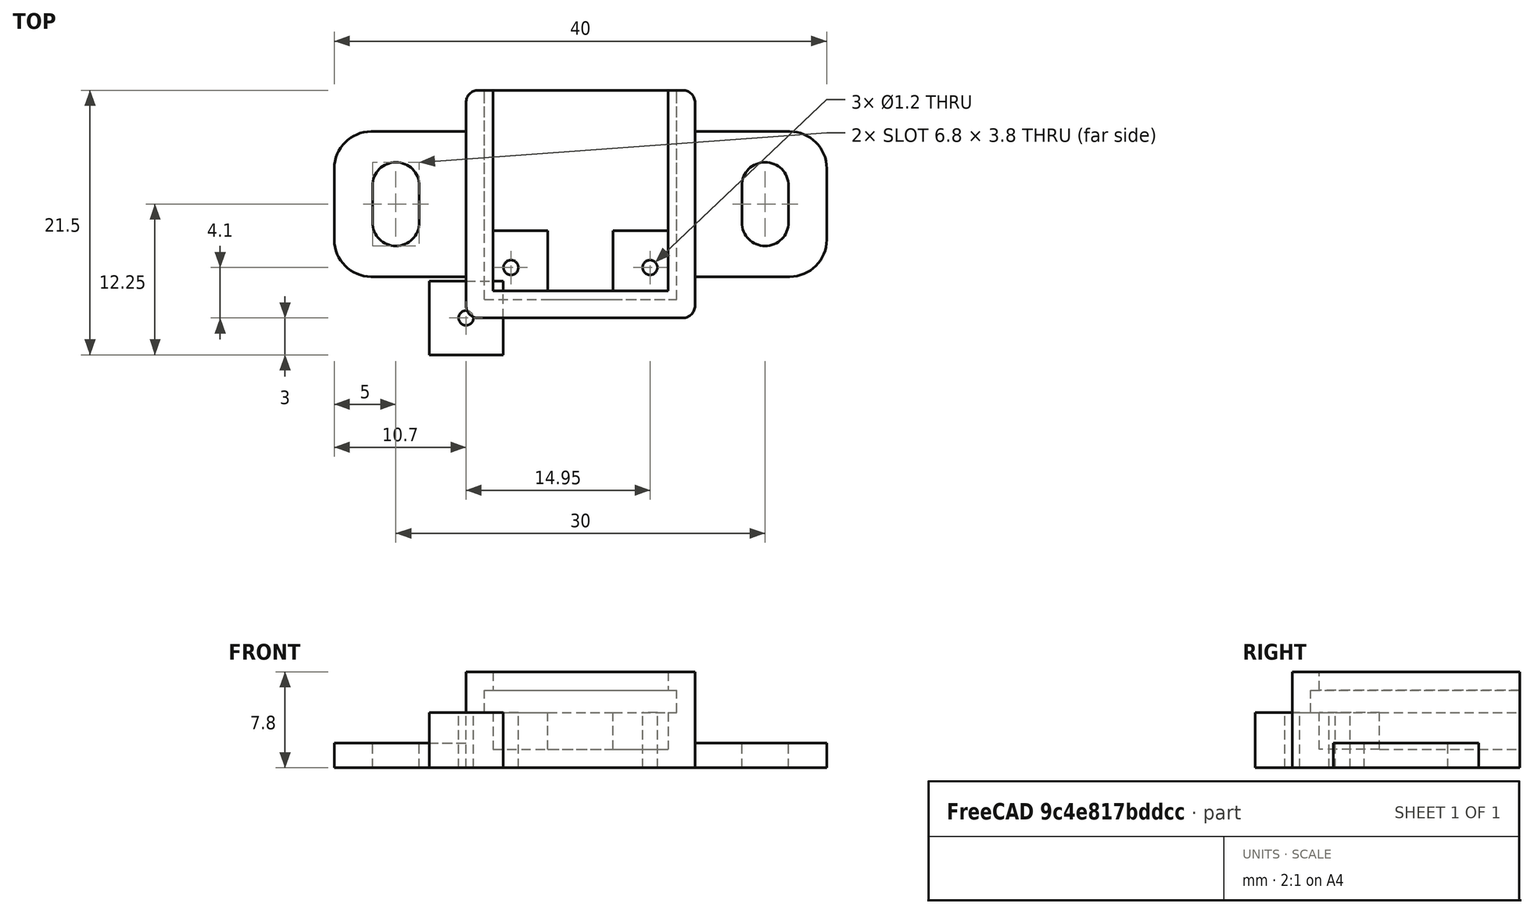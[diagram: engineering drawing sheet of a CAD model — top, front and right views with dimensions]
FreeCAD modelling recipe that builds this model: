
FCSTD DOCUMENT  (FreeCAD 0.19R23578 (Git))
Label: mcp4725_dac
License: FreeArt
LicenseURL: http://artlibre.org/licence/lal
objects: Part::Box×4, Part::MultiFuse×3, Part::Cut×3, Part::FeaturePython×2, Spreadsheet::Sheet×1, Part::Fillet×1, Part::Cylinder×1, Part::Feature×1, App::Part×1
note: 13 computed .brp shape members not serialized (recipe doc carries the construction recipe); baked Part::Feature solids carry a one-line shape summary decoded from their .brp

FEATURE [Spreadsheet::Sheet] Spreadsheet  label="p"
  cells = A1=pcb_x; B1(pcb_x)=15.6; A2=pcb_y; B2(pcb_y)=17; A3=pcb_z; B3(pcb_z)=1.8; A4=pcb_under; B4(pcb_under)=3; A5=side_wall; B5(side_wall)=1.5; A6=pcb_side_lane; B6(pcb_side_lane)=0.7; A7=bottom_wall; B7(bottom_wall)=1.5; A8=pcb_above; B8(pcb_above)=1.5; A9=hole_dist_x; B9(hole_dist_x)=11.3; A10=hole_r; B10(hole_r)=0.6; A11=hole_off_y; B11(hole_off_y)=2.6; A12=hole_stand_size; B12(hole_stand_size)=6
FEATURE [Part::Box] Box  label="external cube"
  AttacherType = Attacher::AttachEngine3D
  Height = 7.8
  Length = 18.6
  Width = 18.5
  expr: Length = <<p>>.pcb_x + 2 * <<p>>.side_wall
  expr: Width = <<p>>.pcb_y + <<p>>.side_wall
  expr: Height = <<p>>.bottom_wall + <<p>>.pcb_under + <<p>>.pcb_z + <<p>>.pcb_above
FEATURE [Part::Box] Box006  label="internal cube"
  AttacherType = Attacher::AttachEngine3D
  Height = 6.3
  Length = 14.2
  Placement = pos=(2.2,2.2,1.5) rot=(0,0,1;0rad)
  Width = 17.1
  expr: Length = <<p>>.pcb_x - 2 * <<p>>.pcb_side_lane
  expr: Width = <<p>>.pcb_y - 2 * <<p>>.pcb_side_lane + <<p>>.side_wall
  expr: Height = <<p>>.pcb_under + <<p>>.pcb_z + <<p>>.pcb_above
  expr: .Placement.Base.z = <<p>>.bottom_wall
  expr: .Placement.Base.x = <<p>>.side_wall + <<p>>.pcb_side_lane
  expr: .Placement.Base.y = <<p>>.side_wall + <<p>>.pcb_side_lane
FEATURE [Part::Box] Box007  label="pcb extract cube"
  AttacherType = Attacher::AttachEngine3D
  Height = 1.8
  Length = 15.6
  Placement = pos=(1.5,1.5,4.5) rot=(0,0,1;0rad)
  Width = 17
  expr: Height = <<p>>.pcb_z
  expr: .Placement.Base.z = <<p>>.bottom_wall + <<p>>.pcb_under
  expr: Width = <<p>>.pcb_y
  expr: Length = <<p>>.pcb_x
  expr: .Placement.Base.x = <<p>>.side_wall
  expr: .Placement.Base.y = <<p>>.side_wall
FEATURE [Part::MultiFuse] Fusion  label="extract fusion"
  Shapes = -> [Box006,Box007]
FEATURE [Part::Fillet] Fillet  label="external fillet"
  Base = -> Box
  Edges = 4 edges r=1: [Edge1,Edge3,Edge5,Edge7]
FEATURE [Part::Cylinder] Cylinder  label="hole"
  Angle = 360
  AttacherType = Attacher::AttachEngine3D
  Height = 10
  Radius = 0.6
  expr: Radius = <<p>>.hole_r
FEATURE [Part::Box] Box008  label="stand"
  AttacherType = Attacher::AttachEngine3D
  Height = 4.5
  Length = 6
  Placement = pos=(-3,-3,0) rot=(0,0,1;0rad)
  Width = 6
  expr: .Placement.Base.y = -<<p>>.hole_stand_size / 2
  expr: .Placement.Base.x = -<<p>>.hole_stand_size / 2
  expr: Width = <<p>>.hole_stand_size
  expr: Length = <<p>>.hole_stand_size
  expr: Height = <<p>>.pcb_under + <<p>>.bottom_wall
FEATURE [Part::FeaturePython] Array  label="hole array"  # Draft array (typed FeaturePython)
  Angle = 360
  ArrayType = 0
  Axis = (0,0,1)
  Base = -> Box008
  Center = (0,0,0)
  Count = 2
  ExpandArray = false
  Fuse = false
  IntervalAxis = (0,0,0)
  IntervalX = (11.3,0,0)
  IntervalY = (0,1,0)
  IntervalZ = (0,0,100)
  NumberCircles = 3
  NumberPolar = 5
  NumberX = 2
  NumberY = 1
  NumberZ = 1
  Placement = pos=(3.65,4.1,0) rot=(0,0,1;0rad)
  PlacementList = 2 placements: [(-3,-3,0),(8.3,-3,0)]
  RadialDistance = 50
  ScaleList = (2) [(1,1,1),(1,1,1)]
  Symmetry = 1
  TangentialDistance = 25
  expr: .IntervalX.x = Spreadsheet.hole_dist_x
  expr: .Placement.Base.x = (2 * <<p>>.side_wall + <<p>>.pcb_x - Spreadsheet.hole_dist_x) / 2
  expr: .Placement.Base.y = Spreadsheet.hole_off_y + <<p>>.side_wall
FEATURE [Part::Cut] Cut003002  label="stand hole cut"
  Base = -> Box008
  Tool = -> Cylinder
FEATURE [Part::FeaturePython] Array001  label="hole array001"  # Draft array (typed FeaturePython)
  Angle = 360
  ArrayType = 0
  Axis = (0,0,1)
  Base = -> Cylinder
  Center = (0,0,0)
  Count = 2
  ExpandArray = false
  Fuse = false
  IntervalAxis = (0,0,0)
  IntervalX = (11.3,0,0)
  IntervalY = (0,1,0)
  IntervalZ = (0,0,100)
  NumberCircles = 3
  NumberPolar = 5
  NumberX = 2
  NumberY = 1
  NumberZ = 1
  Placement = pos=(3.65,4.1,0) rot=(0,0,1;0rad)
  PlacementList = 2 placements: [(0,0,0),(11.3,0,0)]
  RadialDistance = 50
  ScaleList = (2) [(1,1,1),(1,1,1)]
  Symmetry = 1
  TangentialDistance = 25
  expr: .Placement.Base.y = Spreadsheet.hole_off_y + <<p>>.side_wall
  expr: .Placement.Base.x = (2 * <<p>>.side_wall + <<p>>.pcb_x - Spreadsheet.hole_dist_x) / 2
  expr: .IntervalX.x = Spreadsheet.hole_dist_x
FEATURE [Part::Feature] Cut003004  label="attach plane x dir002"
  Placement = pos=(-10.7,3.35,0) rot=(0,0,1;0rad)
  shape: bbox 40 x 11.8 x 2 mm, 18 faces (baked)
FEATURE [Part::MultiFuse] Fusion001  label="body fusion"
  Shapes = -> [Fillet,Cut003004]
FEATURE [Part::Cut] Cut  label="d4184a cut"
  Base = -> Fusion001
  Tool = -> Fusion
FEATURE [Part::MultiFuse] Fusion002  label="mosfet fusion"
  Shapes = -> [Array,Cut]
FEATURE [Part::Cut] Cut003003  label="body cut"
  Base = -> Fusion002
  Tool = -> Array001
FEATURE [App::Part] Part  label="mcp4725 dac pcb box part"
  Group = -> [Box,Fillet,Fusion001,Fusion,Box007,Box006,Cut,Cylinder,Box008,Cut003002,Array,Fusion002,Array001,Cut003003]
  Origin = -> Origin
